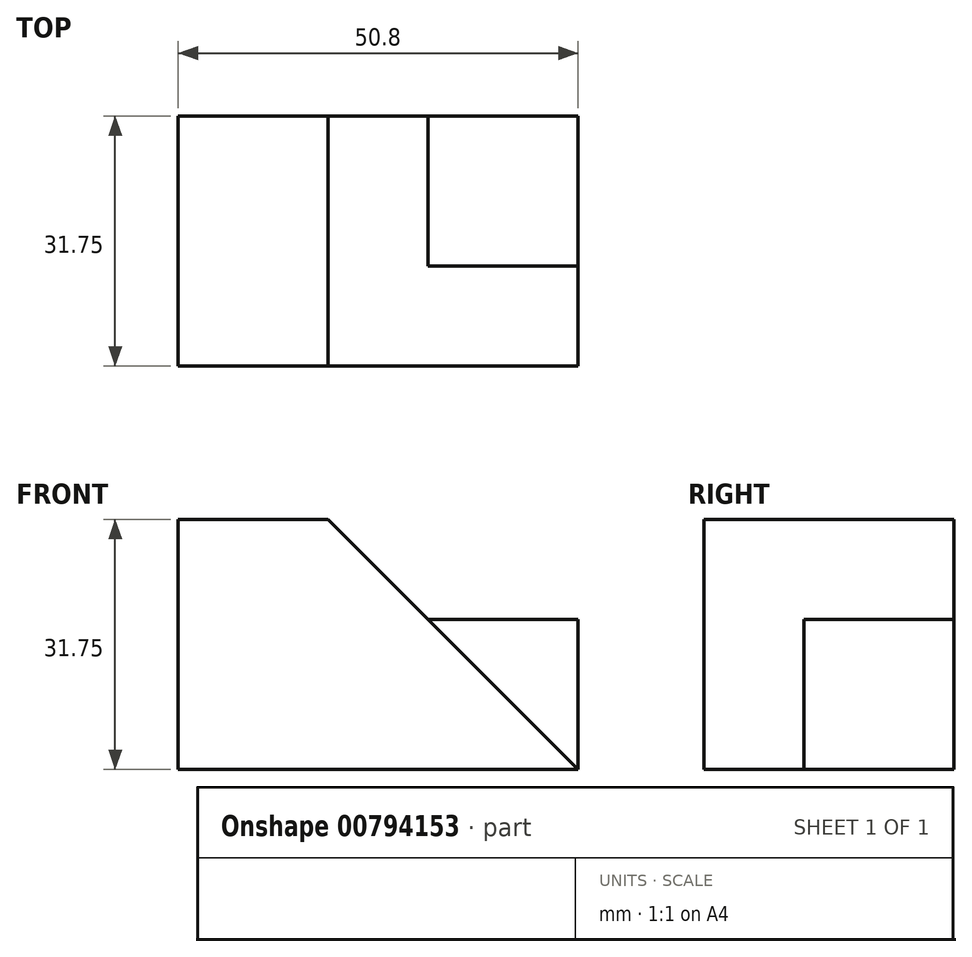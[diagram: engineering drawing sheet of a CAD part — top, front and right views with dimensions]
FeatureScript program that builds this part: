
annotation { "Feature Type Name" : "Feature", "Feature Type Description" : "" }
export const myFeature = defineFeature(function(context is Context, id is Id, definition is map)
    precondition{}
    {
        {
            var Q0;
            Q0=qCreatedBy(makeId("Front.planeOp"),FACE);
            var sketch = newSketch(context, id + "F0", { "sketchPlane" : qUnion([Q0])});
            skLineSegment(sketch, "E0", {"start": v(0, 0) * mm, "end": v(0, 31.75) * mm});
            skLineSegment(sketch, "E1", {"start": v(0, 0) * mm, "end": v(50.8, 0) * mm});
            skLineSegment(sketch, "E2", {"start": v(0, 31.75) * mm, "end": v(50.8, 31.75) * mm});
            skLineSegment(sketch, "E3", {"start": v(50.8, 31.75) * mm, "end": v(50.8, 0) * mm});
            skSolve(sketch);
        }
        {
            var Q0;
            Q0 = qSketchRegion(id + "F0", true);
            extrude(context, id + "F1", {"entities" : qUnion([Q0]), "depth" : 31.75 * mm, "offsetDistance" : 25.4 * mm});
        }
        {
            var Q0;
            Q0=makeQuery(id+"F1.opExtrude","CAP_FACE",FACE,{"disambiguationData":[OSD([sQuery(id+"F0.wireOp",EDGE,"E0"),sQuery(id+"F0.wireOp",EDGE,"E1"),sQuery(id+"F0.wireOp",EDGE,"E2"),sQuery(id+"F0.wireOp",EDGE,"E3")])],"isStart":false});
            var sketch = newSketch(context, id + "F2", { "sketchPlane" : qUnion([Q0])});
            skLineSegment(sketch, "E4", {"start": v(50.8, 31.75) * mm, "end": v(19.05, 31.75) * mm});
            skLineSegment(sketch, "E5", {"start": v(50.8, 31.75) * mm, "end": v(50.8, 0) * mm});
            skLineSegment(sketch, "E6", {"start": v(19.05, 31.75) * mm, "end": v(50.8, 0) * mm});
            skSolve(sketch);
        }
        {
            var Q0;
            Q0=makeQuery(id+"F2.imprint","IMPRINT",FACE,{"disambiguationData":[TD([[makeQuery(id+"F2.imprint","IMPRINT",EDGE,{"derivedFrom":sQuery(id+"F2.wireOp",EDGE,"E4")}),-1.0]])]});
            extrude(context, id + "F3", {"entities" : qUnion([Q0]), "operationType" : NewBodyOperationType.REMOVE, "oppositeDirection" : true, "depth" : 12.7 * mm, "offsetDistance" : 25.4 * mm});
        }
        {
            var Q0;
            Q0=makeQuery(id+"F3.boolean.opBoolean","COPY",FACE,{"derivedFrom":makeQuery(id+"F3.opExtrude","CAP_FACE",FACE,{"disambiguationData":[OSD([sQuery(id+"F2.wireOp",EDGE,"E4"),sQuery(id+"F2.wireOp",EDGE,"E5"),sQuery(id+"F2.wireOp",EDGE,"E6")])],"isStart":false})});
            var sketch = newSketch(context, id + "F4", { "sketchPlane" : qUnion([Q0])});
            skLineSegment(sketch, "E7", {"start": v(19.05, 31.75) * mm, "end": v(50.8, 31.75) * mm});
            skLineSegment(sketch, "E8", {"start": v(50.8, 31.75) * mm, "end": v(50.8, 19.05) * mm});
            skLineSegment(sketch, "E9", {"start": v(50.8, 19.05) * mm, "end": v(31.75, 19.05) * mm});
            skLineSegment(sketch, "E10", {"start": v(31.75, 19.05) * mm, "end": v(19.63, 31.17) * mm});
            skSolve(sketch);
        }
        {
            var Q0;
            {var subQ1=sQuery(id+"F4.wireOp",EDGE,"E7");Q0=makeQuery(id+"F4.imprint","IMPRINT",FACE,{"disambiguationData":[TD([[makeQuery(id+"F4.imprint","IMPRINT",EDGE,{"derivedFrom":subQ1}),-1.0]])]});}
            extrude(context, id + "F5", {"entities" : qUnion([Q0]), "operationType" : NewBodyOperationType.REMOVE, "oppositeDirection" : true, "depth" : 19.05 * mm, "offsetDistance" : 25.4 * mm});
        }
    });
